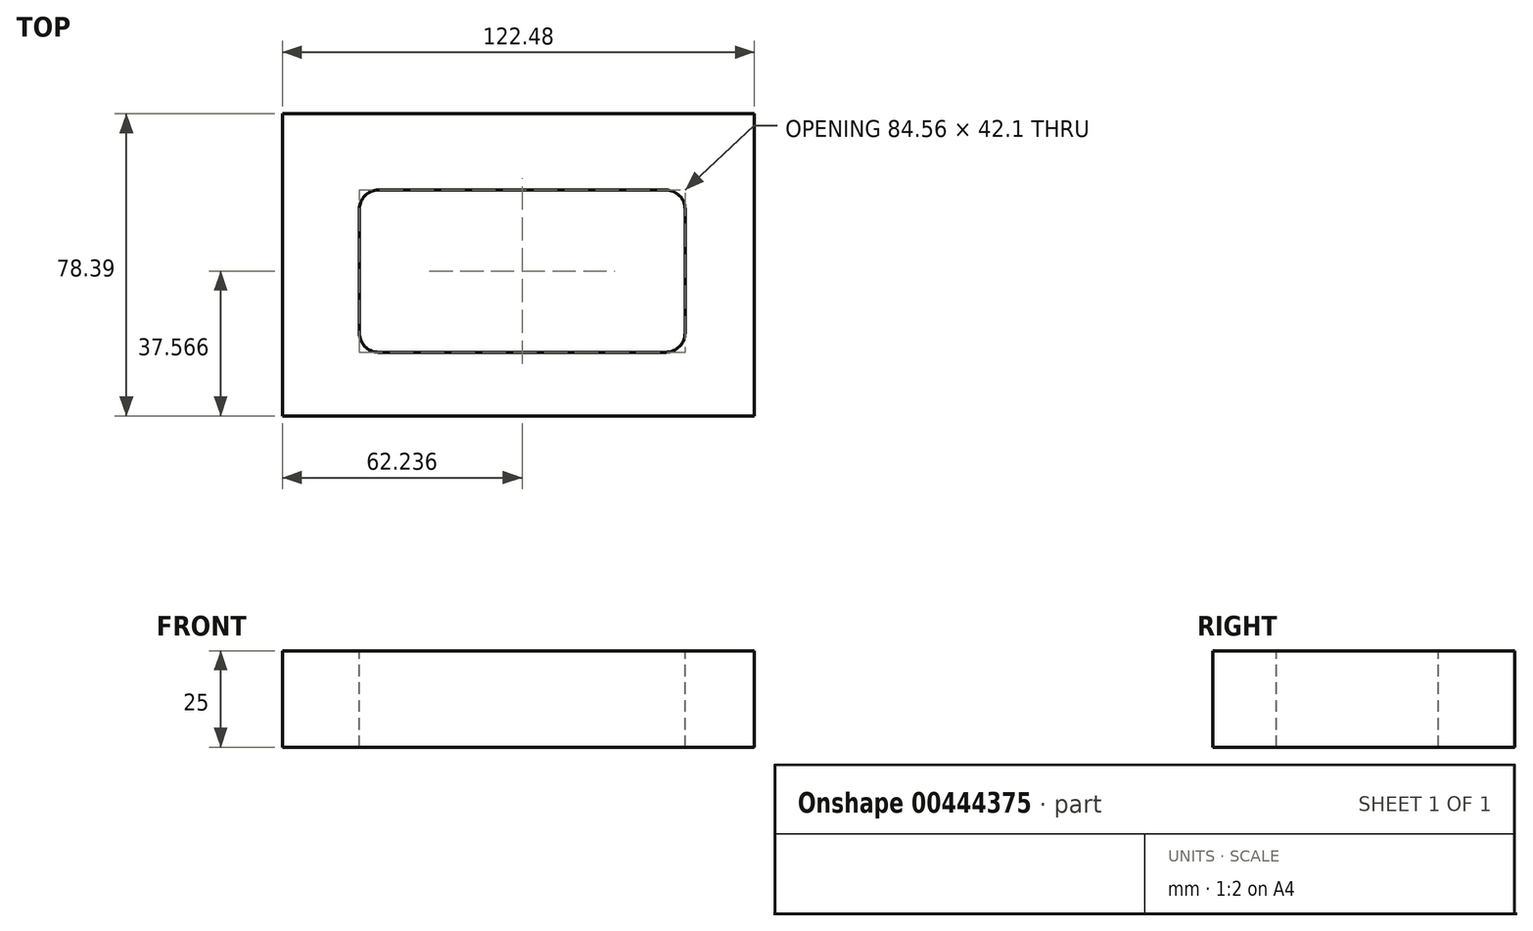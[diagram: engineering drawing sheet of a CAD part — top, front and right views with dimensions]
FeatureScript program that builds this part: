
annotation { "Feature Type Name" : "Feature", "Feature Type Description" : "" }
export const myFeature = defineFeature(function(context is Context, id is Id, definition is map)
    precondition{}
    {
        {
            var Q0;
            Q0=qCreatedBy(makeId("Top.planeOp"),FACE);
            var sketch = newSketch(context, id + "F0", { "sketchPlane" : qUnion([Q0])});
            skLineSegment(sketch, "E0.bottom", {"start": v(-60.24, 39.01) * mm, "end": v(62.24, 39.01) * mm});
            skLineSegment(sketch, "E0.top", {"start": v(-60.24, -39.38) * mm, "end": v(62.24, -39.38) * mm});
            skLineSegment(sketch, "E0.left", {"start": v(-60.24, 39.01) * mm, "end": v(-60.24, -39.38) * mm});
            skLineSegment(sketch, "E0.right", {"start": v(62.24, 39.01) * mm, "end": v(62.24, -39.38) * mm});
            skSolve(sketch);
        }
        {
            var Q0;
            Q0=makeQuery(id+"F0.imprint","IMPRINT",FACE,{"disambiguationData":[TD([[makeQuery(id+"F0.imprint","IMPRINT",EDGE,{"derivedFrom":sQuery(id+"F0.wireOp",EDGE,"E0.bottom")}),-1.0]])]});
            extrude(context, id + "F1", {"entities" : qUnion([Q0]), "depth" : 25 * mm});
        }
        {
            var Q0;
            Q0=makeQuery(id+"F1.opExtrude","CAP_FACE",FACE,{"disambiguationData":[OSD([sQuery(id+"F0.wireOp",EDGE,"E0.bottom"),sQuery(id+"F0.wireOp",EDGE,"E0.top"),sQuery(id+"F0.wireOp",EDGE,"E0.left"),sQuery(id+"F0.wireOp",EDGE,"E0.right")])],"isStart":false});
            var sketch = newSketch(context, id + "F2", { "sketchPlane" : qUnion([Q0])});
            skLineSegment(sketch, "E1.bottom", {"start": v(-40.28, 19.23) * mm, "end": v(44.27, 19.23) * mm});
            skLineSegment(sketch, "E1.top", {"start": v(-40.28, -22.86) * mm, "end": v(44.27, -22.86) * mm});
            skLineSegment(sketch, "E1.left", {"start": v(-40.28, 19.23) * mm, "end": v(-40.28, -22.86) * mm});
            skLineSegment(sketch, "E1.right", {"start": v(44.27, 19.23) * mm, "end": v(44.27, -22.86) * mm});
            skSolve(sketch);
        }
        {
            var Q0;
            Q0=makeQuery(id+"F2.imprint","IMPRINT",FACE,{"disambiguationData":[TD([[makeQuery(id+"F2.imprint","IMPRINT",EDGE,{"derivedFrom":sQuery(id+"F2.wireOp",EDGE,"E1.bottom")}),-1.0]])]});
            extrude(context, id + "F3", {"entities" : qUnion([Q0]), "operationType" : NewBodyOperationType.REMOVE, "oppositeDirection" : true, "depth" : 25 * mm});
        }
        {
            var Q0;
            Q0=makeQuery(id+"F3.boolean.opBoolean","COPY",EDGE,{"derivedFrom":makeQuery(id+"F3.opExtrude","SWEPT_EDGE",EDGE,{"disambiguationData":[OSD([sQuery(id+"F2.wireOp",EDGE,"E1.bottom"),sQuery(id+"F2.wireOp",EDGE,"E1.left")])]})});
            var Q1;
            Q1=makeQuery(id+"F3.boolean.opBoolean","COPY",EDGE,{"derivedFrom":makeQuery(id+"F3.opExtrude","SWEPT_EDGE",EDGE,{"disambiguationData":[OSD([sQuery(id+"F2.wireOp",EDGE,"E1.bottom"),sQuery(id+"F2.wireOp",EDGE,"E1.right")])]})});
            var Q2;
            Q2=makeQuery(id+"F3.boolean.opBoolean","COPY",EDGE,{"derivedFrom":makeQuery(id+"F3.opExtrude","SWEPT_EDGE",EDGE,{"disambiguationData":[OSD([sQuery(id+"F2.wireOp",EDGE,"E1.top"),sQuery(id+"F2.wireOp",EDGE,"E1.right")])]})});
            var Q3;
            Q3=makeQuery(id+"F3.boolean.opBoolean","COPY",EDGE,{"derivedFrom":makeQuery(id+"F3.opExtrude","SWEPT_EDGE",EDGE,{"disambiguationData":[OSD([sQuery(id+"F2.wireOp",EDGE,"E1.top"),sQuery(id+"F2.wireOp",EDGE,"E1.left")])]})});
            fillet(context, id + "F4", {"entities" : qUnion([Q0, Q1, Q2, Q3]), "radius" : 5 * mm, "tangentPropagation" : true, "allowEdgeOverflow" : false});
        }
    });
